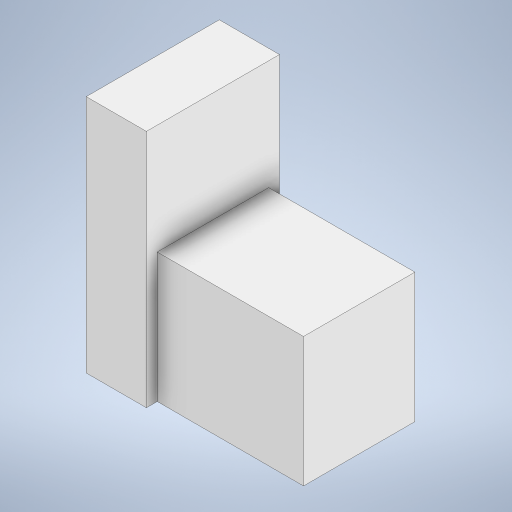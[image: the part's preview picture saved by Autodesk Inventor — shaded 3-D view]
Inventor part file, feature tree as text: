
AUTODESK INVENTOR PART (.ipt)
format: ipt  version: 2024 (Build 280153000, 153)  size: 211,456 bytes
history: native  units: in
note: dims shown in document units (in); Inventor stores cm internally (conversion verified against a paired STEP export)
features: extrude x2, sketch x2
ambient origin geometry x8: Origin, YZ Plane, XZ Plane, XY Plane, X Axis, Y Axis, Z Axis, Center Point
bodies: Solid1 (feature_tree)
feature tree (4):
  extrude  "Extrusion1"  Depth=31.3in
  extrude  "Extrusion2"  Depth=14.57in
  sketch  "Sketch1"  dims[d1=17.4in d2=31.3in]
  sketch  "Sketch2"  dims[d3=7.87in d4=0.0in d5=14.57in d6=16.93in d7=1.415in d8=19.13in d9=0.0in]
